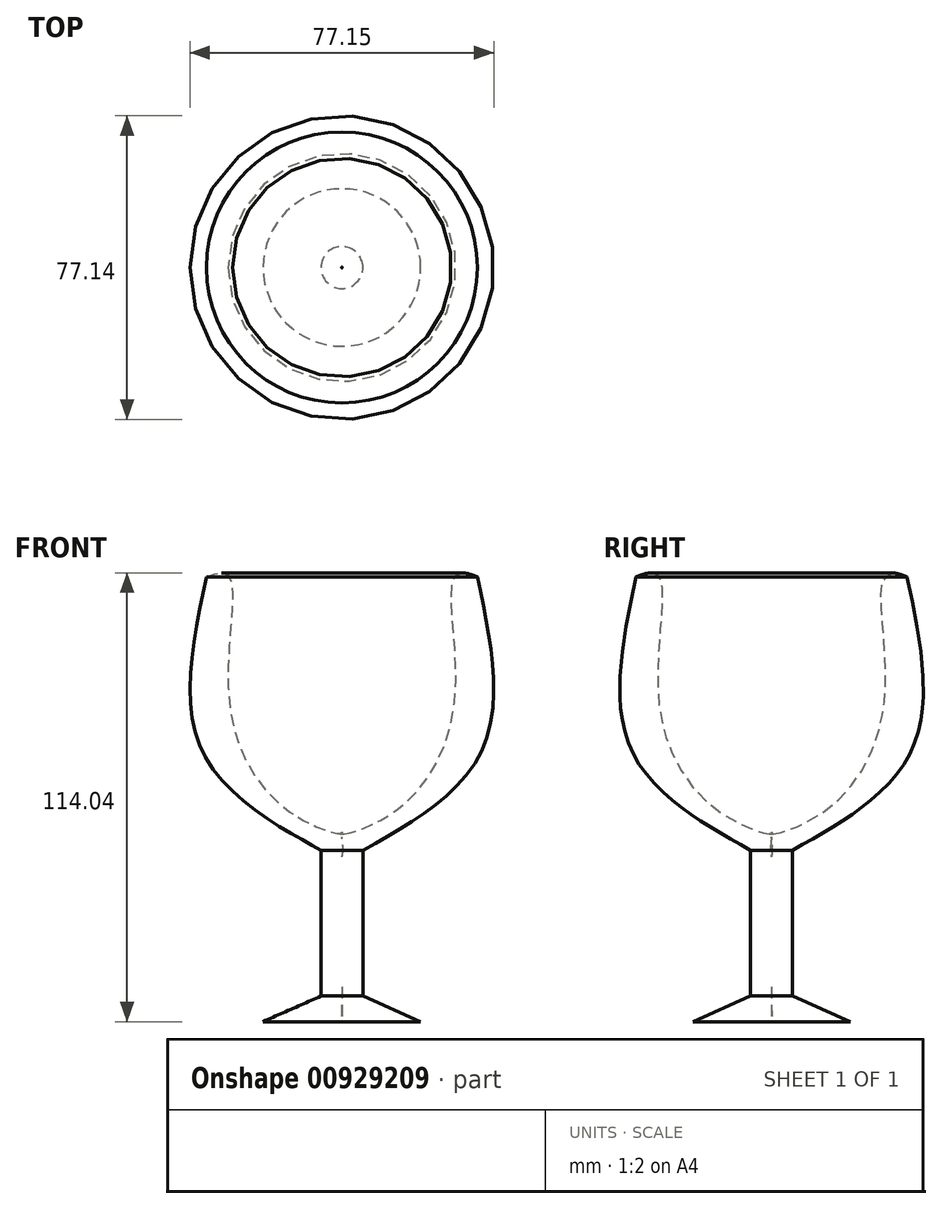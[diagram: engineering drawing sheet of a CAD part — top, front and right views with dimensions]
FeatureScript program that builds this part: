
annotation { "Feature Type Name" : "Feature", "Feature Type Description" : "" }
export const myFeature = defineFeature(function(context is Context, id is Id, definition is map)
    precondition{}
    {
        {
            var Q0;
            Q0=qCreatedBy(makeId("Front.planeOp"),FACE);
            var sketch = newSketch(context, id + "F0", { "sketchPlane" : qUnion([Q0])});
            skFitSpline(sketch, "E0", {"points": [v(-34.35, 40.27) * mm, v(-28.7, 40.54) * mm, v(-28.7, 9.83) * mm, v(-13.07, -19.53) * mm, v(0, -24.92) * mm, v(0, -24.38) * mm], "startDerivative": vector(51.98, 18.73) * mm, "endDerivative": vector(-5.6, 15.84) * mm});
            skFitSpline(sketch, "E1", {"points": [v(-34.35, 40.27) * mm, v(-34.35, -6.06) * mm, v(-5.25, -29.23) * mm, v(0.08, -30.85) * mm, v(0, -24.92) * mm, v(0.08, -24.6) * mm], "startDerivative": vector(-28.93, -136.26) * mm, "endDerivative": vector(3.6, 5.2) * mm});
            skLineSegment(sketch, "E2", {"start": v(0.08, -30.85) * mm, "end": v(0.08, -63.89) * mm});
            skLineSegment(sketch, "E3", {"start": v(-5.25, -66.25) * mm, "end": v(-19.94, -72.77) * mm});
            skLineSegment(sketch, "E4", {"start": v(-19.94, -72.77) * mm, "end": v(0, -72.77) * mm});
            skLineSegment(sketch, "E5", {"start": v(0, -72.77) * mm, "end": v(0.08, -63.89) * mm});
            skLineSegment(sketch, "E6", {"start": v(-5.25, -29.23) * mm, "end": v(-5.25, -66.25) * mm});
            skLineSegment(sketch, "E7", {"start": v(0.08, -24.6) * mm, "end": v(0.08, -30.85) * mm});
            skLineSegment(sketch, "E8", {"start": v(0.08, -24.6) * mm, "end": v(0.08, -15.88) * mm});
            skSolve(sketch);
        }
        {
            var Q0;
            Q0 = qSketchRegion(id + "F0", true);
            var Q1;
            Q1=sQuery(id+"F0.wireOp",EDGE,"E8");
            revolve(context, id + "F1", {"surfaceOperationType" : NewSurfaceOperationType.NEW, "entities" : qUnion([Q0]), "axis" : qUnion([Q1]), "revolveType" : RevolveType.FULL});
        }
    });
